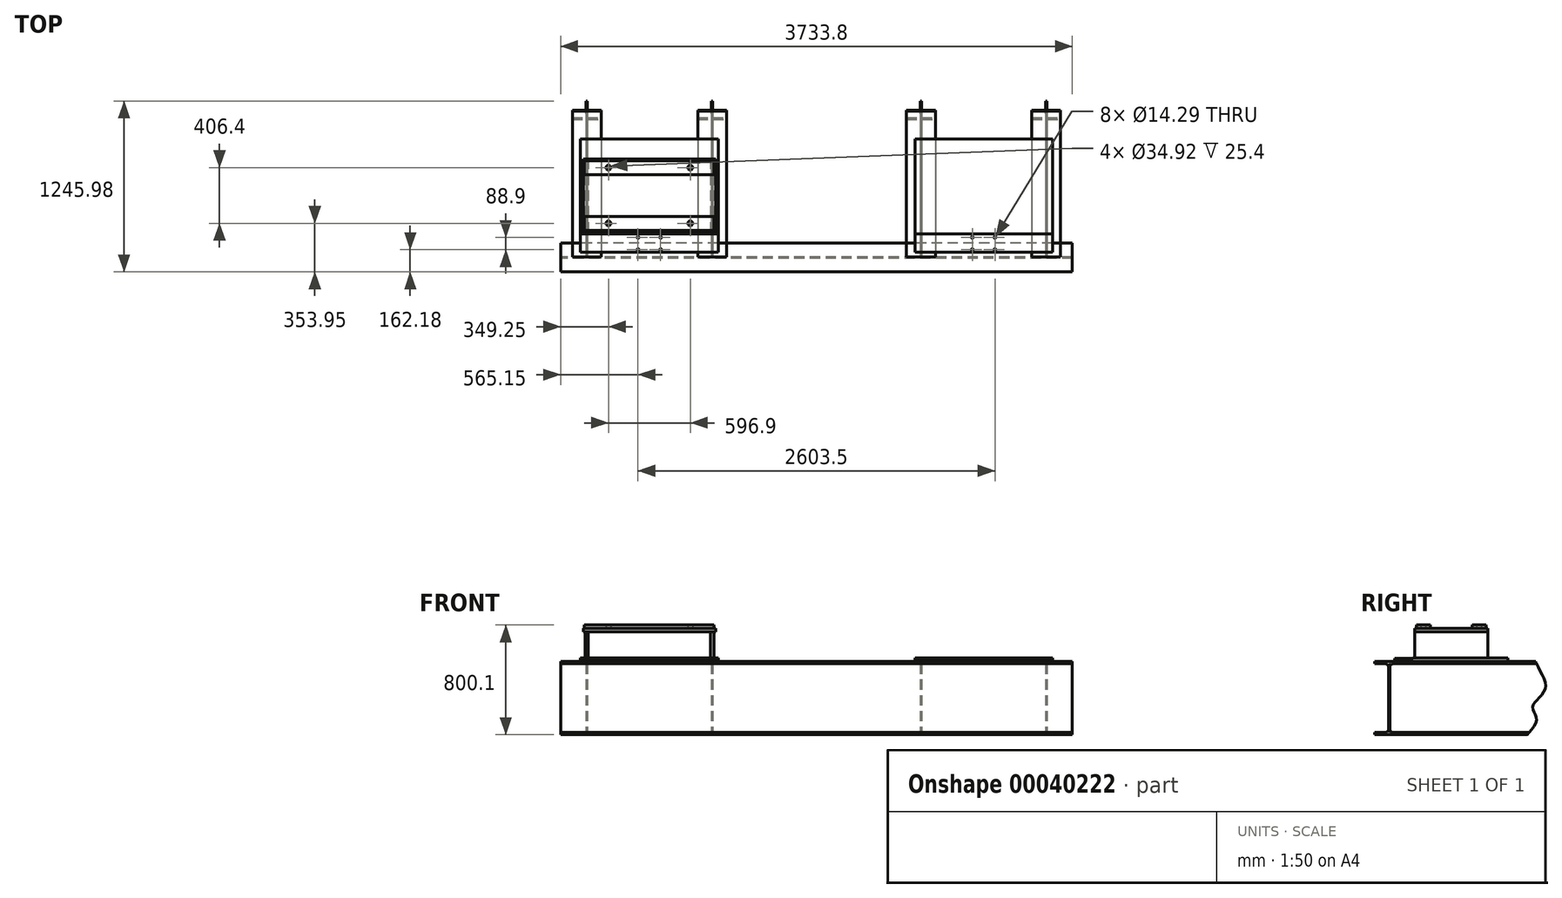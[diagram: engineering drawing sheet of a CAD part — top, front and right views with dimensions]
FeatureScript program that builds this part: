
annotation { "Feature Type Name" : "Feature", "Feature Type Description" : "" }
export const myFeature = defineFeature(function(context is Context, id is Id, definition is map)
    precondition{}
    {
        {
            var Q0;
            Q0=qCreatedBy(makeId("Top.planeOp"),FACE);
            var sketch = newSketch(context, id + "F0", { "sketchPlane" : qUnion([Q0])});
            skLineSegment(sketch, "E0", {"start": v(0, 102.84) * mm, "end": v(0, -93.54) * mm, "construction": true});
            skLineSegment(sketch, "E1.0", {"start": v(-1219.2, 102.84) * mm, "end": v(-1219.2, -93.54) * mm, "construction": true});
            skLineSegment(sketch, "E2", {"start": v(-1060.57, 0) * mm, "end": v(-1402.82, 0) * mm, "construction": true});
            skLineSegment(sketch, "E3.0", {"start": v(-1720.85, 412.75) * mm, "end": v(-1720.85, -412.75) * mm});
            skLineSegment(sketch, "E4.0", {"start": v(-717.55, -412.75) * mm, "end": v(-1720.85, -412.75) * mm});
            skLineSegment(sketch, "E5.MirrorCS", {"start": v(-717.55, 412.75) * mm, "end": v(-717.55, -412.75) * mm});
            skLineSegment(sketch, "E6.MirrorCS", {"start": v(-717.55, 412.75) * mm, "end": v(-1720.85, 412.75) * mm});
            skPoint(sketch, "E7.orphan", {"position": v(-1402.82, -412.75) * mm});
            skPoint(sketch, "E8.orphan", {"position": v(-1402.82, 412.75) * mm});
            skPoint(sketch, "E9.orphan", {"position": v(-1060.57, 412.75) * mm});
            skPoint(sketch, "E10.orphan", {"position": v(-1060.57, -412.75) * mm});
            skPoint(sketch, "E11.orphan", {"position": v(-1720.85, 102.84) * mm});
            skPoint(sketch, "E12.orphan", {"position": v(-1720.85, -93.54) * mm});
            skPoint(sketch, "E13.orphan", {"position": v(-717.55, -93.54) * mm});
            skPoint(sketch, "E14.orphan", {"position": v(-717.55, 102.84) * mm});
            skSolve(sketch);
        }
        {
            var Q0;
            Q0 = qSketchRegion(id + "F0", true);
            extrude(context, id + "F1", {"entities" : qUnion([Q0]), "oppositeDirection" : true, "depth" : 25.4 * mm});
        }
        {
            var Q0;
            Q0=makeQuery(id+"F1.opExtrude","SWEPT_FACE",FACE,{"disambiguationData":[OSD([sQuery(id+"F0.wireOp",EDGE,"E3.0")])]});
            var sketch = newSketch(context, id + "F2", { "sketchPlane" : qUnion([Q0])});
            skLineSegment(sketch, "E15", {"start": v(0, 139.77) * mm, "end": v(0, -170.54) * mm, "construction": true});
            skPoint(sketch, "E15.startSnap0", {"position": v(0, 0) * mm});
            skLineSegment(sketch, "E16.0", {"start": v(-412.75, 0) * mm, "end": v(412.75, 0) * mm, "construction": true});
            skLineSegment(sketch, "E17.0", {"start": v(279.4, 139.77) * mm, "end": v(279.4, -170.54) * mm, "construction": true});
            skLineSegment(sketch, "E18.0", {"start": v(-412.75, -3.18) * mm, "end": v(412.75, -3.18) * mm, "construction": true});
            skLineSegment(sketch, "E19.bottom", {"start": v(279.4, -3.18) * mm, "end": v(422.05, -3.18) * mm});
            skLineSegment(sketch, "E19.top", {"start": v(279.4, 13.88) * mm, "end": v(422.05, 13.88) * mm});
            skLineSegment(sketch, "E19.left", {"start": v(279.4, -3.18) * mm, "end": v(279.4, 13.88) * mm});
            skLineSegment(sketch, "E19.right", {"start": v(422.05, -3.18) * mm, "end": v(422.05, 13.88) * mm});
            skSolve(sketch);
        }
        {
            var Q0;
            Q0 = qSketchRegion(id + "F2", true);
            extrude(context, id + "F3", {"entities" : qUnion([Q0]), "operationType" : NewBodyOperationType.REMOVE, "endBound" : BoundingType.THROUGH_ALL, "oppositeDirection" : true, "depth" : 25.4 * mm});
        }
        {
            var Q0;
            Q0=makeQuery(id+"F0.imprint","IMPRINT",FACE,{"disambiguationData":[TD([[makeQuery(id+"F0.imprint","IMPRINT",EDGE,{"derivedFrom":sQuery(id+"F0.wireOp",EDGE,"E3.0")}),1.0]])]});
            cPlane(context, id + "F4", {"entities" : qUnion([Q0]), "cplaneType" : CPlaneType.OFFSET, "offset" : 215.9 * mm, "width" : 152.4 * mm, "height" : 152.4 * mm});
        }
        {
            var Q0;
            Q0=qCreatedBy(id+"F4.planeOp",FACE);
            var sketch = newSketch(context, id + "F5", { "sketchPlane" : qUnion([Q0])});
            skLineSegment(sketch, "E20.1", {"start": v(-1060.57, 0) * mm, "end": v(-1402.82, 0) * mm, "construction": true});
            skLineSegment(sketch, "E20.2", {"start": v(-1219.2, 102.84) * mm, "end": v(-1219.2, -93.54) * mm, "construction": true});
            skLineSegment(sketch, "E21.0", {"start": v(-736.6, 266.7) * mm, "end": v(-1701.8, 266.7) * mm});
            skLineSegment(sketch, "E22.0", {"start": v(-1701.8, 266.7) * mm, "end": v(-1701.8, -266.7) * mm});
            skLineSegment(sketch, "E23.MirrorCS", {"start": v(-736.6, 266.7) * mm, "end": v(-736.6, -266.7) * mm});
            skLineSegment(sketch, "E24.MirrorCS", {"start": v(-736.6, -266.7) * mm, "end": v(-1701.8, -266.7) * mm});
            skPoint(sketch, "E25.orphan", {"position": v(-1060.57, 266.7) * mm});
            skPoint(sketch, "E26.orphan", {"position": v(-736.6, 102.84) * mm});
            skPoint(sketch, "E27.orphan", {"position": v(-736.6, -93.54) * mm});
            skPoint(sketch, "E28.orphan", {"position": v(-1060.57, -266.7) * mm});
            skPoint(sketch, "E29.orphan", {"position": v(-1402.82, -266.7) * mm});
            skPoint(sketch, "E30.orphan", {"position": v(-1701.8, -93.54) * mm});
            skPoint(sketch, "E31.orphan", {"position": v(-1701.8, 102.84) * mm});
            skPoint(sketch, "E32.orphan", {"position": v(-1402.82, 266.7) * mm});
            skSolve(sketch);
        }
        {
            var Q0;
            Q0 = qSketchRegion(id + "F5", true);
            extrude(context, id + "F6", {"entities" : qUnion([Q0]), "oppositeDirection" : true, "depth" : 25.4 * mm});
        }
        {
            var Q0;
            Q0=makeQuery(id+"F6.opExtrude","CAP_FACE",FACE,{"disambiguationData":[OSD([sQuery(id+"F5.wireOp",EDGE,"E21.0"),sQuery(id+"F5.wireOp",EDGE,"E22.0"),sQuery(id+"F5.wireOp",EDGE,"E23.MirrorCS"),sQuery(id+"F5.wireOp",EDGE,"E24.MirrorCS")])],"isStart":true});
            var sketch = newSketch(context, id + "F7", { "sketchPlane" : qUnion([Q0])});
            skLineSegment(sketch, "E33", {"start": v(-736.6, 0) * mm, "end": v(-1701.8, 0) * mm, "construction": true});
            skLineSegment(sketch, "E34", {"start": v(-1219.2, 266.7) * mm, "end": v(-1219.2, -266.7) * mm, "construction": true});
            skLineSegment(sketch, "E35.0", {"start": v(-736.6, 152.4) * mm, "end": v(-1701.8, 152.4) * mm, "construction": true});
            skLineSegment(sketch, "E36.0", {"start": v(-736.6, 254) * mm, "end": v(-1701.8, 254) * mm, "construction": true});
            skLineSegment(sketch, "E37.0", {"start": v(-1692.27, 266.7) * mm, "end": v(-1692.27, -266.7) * mm, "construction": true});
            skLineSegment(sketch, "E38.bottom", {"start": v(-1692.27, 254) * mm, "end": v(-746.12, 254) * mm});
            skLineSegment(sketch, "E38.top", {"start": v(-1692.27, 152.4) * mm, "end": v(-746.12, 152.4) * mm});
            skLineSegment(sketch, "E38.left", {"start": v(-1692.27, 254) * mm, "end": v(-1692.27, 152.4) * mm});
            skLineSegment(sketch, "E38.right", {"start": v(-746.12, 254) * mm, "end": v(-746.12, 152.4) * mm});
            skLineSegment(sketch, "E39.MirrorCS", {"start": v(-736.6, -254) * mm, "end": v(-1701.8, -254) * mm});
            skLineSegment(sketch, "E40.MirrorCS", {"start": v(-736.6, -152.4) * mm, "end": v(-1701.8, -152.4) * mm});
            skLineSegment(sketch, "E41.MirrorCS", {"start": v(-1692.27, -254) * mm, "end": v(-1692.27, -152.4) * mm});
            skLineSegment(sketch, "E42.MirrorCS", {"start": v(-1692.27, -152.4) * mm, "end": v(-746.12, -152.4) * mm});
            skLineSegment(sketch, "E43.MirrorCS", {"start": v(-1692.27, -254) * mm, "end": v(-746.12, -254) * mm});
            skLineSegment(sketch, "E44.MirrorCS", {"start": v(-746.12, -254) * mm, "end": v(-746.12, -152.4) * mm});
            skLineSegment(sketch, "E45", {"start": v(-1692.27, 203.2) * mm, "end": v(-746.12, 203.2) * mm, "construction": true});
            skLineSegment(sketch, "E46.0", {"start": v(-1517.65, 266.7) * mm, "end": v(-1517.65, -266.7) * mm, "construction": true});
            skCircle(sketch, "E47", {"center": v(-1517.65, 203.2) * mm, "radius": 17.46 * mm});
            skCircle(sketch, "E48.MirrorC", {"center": v(-920.75, 203.2) * mm, "radius": 17.46 * mm});
            skCircle(sketch, "E49.MirrorC", {"center": v(-920.75, -203.2) * mm, "radius": 17.46 * mm});
            skCircle(sketch, "E50.MirrorC", {"center": v(-1517.65, -203.2) * mm, "radius": 17.46 * mm});
            skSolve(sketch);
        }
        {
            var Q0;
            Q0 = qSketchRegion(id + "F7", true);
            extrude(context, id + "F8", {"entities" : qUnion([Q0]), "operationType" : NewBodyOperationType.ADD, "depth" : 25.4 * mm});
        }
        {
            var Q0;
            Q0=makeQuery(id+"F0.imprint","IMPRINT",FACE,{"disambiguationData":[TD([[makeQuery(id+"F0.imprint","IMPRINT",EDGE,{"derivedFrom":sQuery(id+"F0.wireOp",EDGE,"E3.0")}),1.0]])]});
            var sketch = newSketch(context, id + "F9", { "sketchPlane" : qUnion([Q0])});
            skLineSegment(sketch, "E51.0", {"start": v(-1219.2, 102.84) * mm, "end": v(-1219.2, -93.54) * mm, "construction": true});
            skLineSegment(sketch, "E52.0", {"start": v(-736.6, 266.7) * mm, "end": v(-1701.8, 266.7) * mm, "construction": true});
            skLineSegment(sketch, "E53.0", {"start": v(-736.6, -266.7) * mm, "end": v(-1701.8, -266.7) * mm, "construction": true});
            skLineSegment(sketch, "E54.0", {"start": v(-1663.7, 266.7) * mm, "end": v(-1663.7, -93.54) * mm, "construction": true});
            skLineSegment(sketch, "E55.0", {"start": v(-1689.1, 102.84) * mm, "end": v(-1689.1, -93.54) * mm, "construction": true});
            skLineSegment(sketch, "E56.bottom", {"start": v(-1663.7, 266.7) * mm, "end": v(-1689.1, 266.7) * mm});
            skLineSegment(sketch, "E56.top", {"start": v(-1663.7, -266.7) * mm, "end": v(-1689.1, -266.7) * mm});
            skLineSegment(sketch, "E56.left", {"start": v(-1663.7, 266.7) * mm, "end": v(-1663.7, -266.7) * mm});
            skLineSegment(sketch, "E56.right", {"start": v(-1689.1, 266.7) * mm, "end": v(-1689.1, -266.7) * mm});
            skLineSegment(sketch, "E57.MirrorCS", {"start": v(-774.7, -266.7) * mm, "end": v(-749.3, -266.7) * mm});
            skLineSegment(sketch, "E58.MirrorCS", {"start": v(-774.7, 266.7) * mm, "end": v(-749.3, 266.7) * mm});
            skLineSegment(sketch, "E59.MirrorCS", {"start": v(-749.3, 102.84) * mm, "end": v(-749.3, -93.54) * mm});
            skLineSegment(sketch, "E60.MirrorCS", {"start": v(-774.7, 266.7) * mm, "end": v(-774.7, -93.54) * mm});
            skLineSegment(sketch, "E61.MirrorCS", {"start": v(-749.3, 266.7) * mm, "end": v(-749.3, -266.7) * mm});
            skLineSegment(sketch, "E62.MirrorCS", {"start": v(-774.7, 266.7) * mm, "end": v(-774.7, -266.7) * mm});
            skSolve(sketch);
        }
        {
            var Q0;
            Q0 = qSketchRegion(id + "F9", true);
            var Q1;
            Q1=makeQuery(id+"F6.opExtrude","CAP_FACE",FACE,{"disambiguationData":[OSD([sQuery(id+"F5.wireOp",EDGE,"E21.0"),sQuery(id+"F5.wireOp",EDGE,"E22.0"),sQuery(id+"F5.wireOp",EDGE,"E23.MirrorCS"),sQuery(id+"F5.wireOp",EDGE,"E24.MirrorCS")])],"isStart":false});
            extrude(context, id + "F10", {"entities" : qUnion([Q0]), "endBound" : BoundingType.UP_TO_SURFACE, "endBoundEntityFace" : qUnion([Q1]), "depth" : 25.4 * mm});
        }
        {
            var Q0;
            Q0=makeQuery(id+"F0.imprint","IMPRINT",FACE,{"disambiguationData":[TD([[makeQuery(id+"F0.imprint","IMPRINT",EDGE,{"derivedFrom":sQuery(id+"F0.wireOp",EDGE,"E3.0")}),1.0]])]});
            var sketch = newSketch(context, id + "F11", { "sketchPlane" : qUnion([Q0])});
            skLineSegment(sketch, "E63.0", {"start": v(-1219.2, 102.84) * mm, "end": v(-1219.2, -412.75) * mm, "construction": true});
            skLineSegment(sketch, "E64.0", {"start": v(-717.55, -412.75) * mm, "end": v(-1720.85, -412.75) * mm, "construction": true});
            skPoint(sketch, "E65.orphan", {"position": v(-1219.2, -93.54) * mm});
            skLineSegment(sketch, "E66.0", {"start": v(-1060.57, 0) * mm, "end": v(-1402.82, 0) * mm, "construction": true});
            skLineSegment(sketch, "E67.0", {"start": v(-1060.57, -306.07) * mm, "end": v(-1402.82, -306.07) * mm, "construction": true});
            skLineSegment(sketch, "E68.0", {"start": v(-1060.57, -394.97) * mm, "end": v(-1402.82, -394.97) * mm, "construction": true});
            skLineSegment(sketch, "E69.0", {"start": v(-1301.75, 102.84) * mm, "end": v(-1301.75, -412.75) * mm, "construction": true});
            skLineSegment(sketch, "E70.0", {"start": v(-1136.65, 102.84) * mm, "end": v(-1136.65, -412.75) * mm, "construction": true});
            skPoint(sketch, "E71", {"position": v(-1136.65, -306.07) * mm});
            skPoint(sketch, "E72", {"position": v(-1136.65, -394.97) * mm});
            skPoint(sketch, "E73", {"position": v(-1301.75, -394.97) * mm});
            skPoint(sketch, "E74", {"position": v(-1301.75, -306.07) * mm});
            skSolve(sketch);
        }
        {
            var Q0;
            Q0=sQuery(id+"F11.wireOp",VERTEX,"E71");
            var Q1;
            Q1=sQuery(id+"F11.wireOp",VERTEX,"E72");
            var Q2;
            Q2=sQuery(id+"F11.wireOp",VERTEX,"E74");
            var Q3;
            Q3=sQuery(id+"F11.wireOp",VERTEX,"E73");
            var Q4;
            Q4=makeQuery(id+"F1.opExtrude","SWEPT_BODY",BODY,{"disambiguationData":[OSD([sQuery(id+"F0.wireOp",EDGE,"E3.0"),sQuery(id+"F0.wireOp",EDGE,"E4.0"),sQuery(id+"F0.wireOp",EDGE,"E5.MirrorCS"),sQuery(id+"F0.wireOp",EDGE,"E6.MirrorCS")])]});
            hole(context, id + "F12", {"style" : HoleStyle.SIMPLE, "holeDiameter" : 14.29 * mm, "endStyle" : HoleEndStyle.THROUGH, "locations" : qUnion([Q0, Q1, Q2, Q3]), "scope" : qUnion([Q4])});
        }
        {
            var Q0;
            Q0=qCreatedBy(makeId("Right.planeOp"),FACE);
            var sketch = newSketch(context, id + "F13", { "sketchPlane" : qUnion([Q0])});
            skLineSegment(sketch, "E75", {"start": v(0, 291.52) * mm, "end": v(0, -174.65) * mm, "construction": true});
            skLineSegment(sketch, "E76.0", {"start": v(-452.37, -25.4) * mm, "end": v(-452.37, -558.8) * mm, "construction": true});
            skLineSegment(sketch, "E77.0", {"start": v(412.75, -25.4) * mm, "end": v(-452.37, -25.4) * mm, "construction": true});
            skPoint(sketch, "E78.orphan", {"position": v(-412.75, -25.4) * mm});
            skLineSegment(sketch, "E79.0", {"start": v(-347.6, -558.8) * mm, "end": v(-452.37, -558.8) * mm});
            skLineSegment(sketch, "E80.0", {"start": v(-347.6, 291.52) * mm, "end": v(-347.6, -41.02) * mm});
            skLineSegment(sketch, "E81.bottom", {"start": v(-347.6, -558.8) * mm, "end": v(-557.15, -558.8) * mm});
            skLineSegment(sketch, "E81.top", {"start": v(-347.6, -25.4) * mm, "end": v(-557.15, -25.4) * mm});
            skLineSegment(sketch, "E81.left", {"start": v(-347.6, -558.8) * mm, "end": v(-347.6, -543.18) * mm});
            skLineSegment(sketch, "E81.right", {"start": v(-557.15, -558.8) * mm, "end": v(-557.15, -543.18) * mm});
            skLineSegment(sketch, "E82.0", {"start": v(-347.6, -41.02) * mm, "end": v(-421.9, -41.02) * mm});
            skLineSegment(sketch, "E83.0", {"start": v(-347.6, -543.18) * mm, "end": v(-421.9, -543.18) * mm});
            skLineSegment(sketch, "E84.1", {"start": v(-457.45, -66.42) * mm, "end": v(-457.45, -517.78) * mm});
            skLineSegment(sketch, "E85.1", {"start": v(-447.3, -66.42) * mm, "end": v(-447.3, -517.78) * mm});
            skLineSegment(sketch, "E86.trimOffspring", {"start": v(-557.15, -41.02) * mm, "end": v(-557.15, -25.4) * mm});
            skLineSegment(sketch, "E87.trimOffspring", {"start": v(-482.85, -41.02) * mm, "end": v(-557.15, -41.02) * mm});
            skLineSegment(sketch, "E88.trimOffspring", {"start": v(-347.6, -543.18) * mm, "end": v(-347.6, -558.8) * mm});
            skLineSegment(sketch, "E89.trimOffspring", {"start": v(-347.6, -41.02) * mm, "end": v(-347.6, -25.4) * mm});
            skLineSegment(sketch, "E90.trimOffspring", {"start": v(-482.85, -543.18) * mm, "end": v(-557.15, -543.18) * mm});
            skPoint(sketch, "E91.visualSharp", {"position": v(-457.45, -41.02) * mm});
            skArc(sketch, "E91.filletArc", {"start": v(-457.45, -66.42) * mm, "mid": v(-464.9, -48.46) * mm, "end": v(-482.85, -41.02) * mm});
            skPoint(sketch, "E92.visualSharp", {"position": v(-447.3, -41.02) * mm});
            skArc(sketch, "E92.filletArc", {"start": v(-421.9, -41.02) * mm, "mid": v(-439.85, -48.46) * mm, "end": v(-447.3, -66.42) * mm});
            skPoint(sketch, "E93.visualSharp", {"position": v(-457.45, -543.18) * mm});
            skArc(sketch, "E93.filletArc", {"start": v(-482.85, -543.18) * mm, "mid": v(-464.9, -535.74) * mm, "end": v(-457.45, -517.78) * mm});
            skPoint(sketch, "E94.visualSharp", {"position": v(-447.3, -543.18) * mm});
            skArc(sketch, "E94.filletArc", {"start": v(-447.3, -517.78) * mm, "mid": v(-439.85, -535.74) * mm, "end": v(-421.9, -543.18) * mm});
            skSolve(sketch);
        }
        {
            var Q0;
            Q0 = qSketchRegion(id + "F13", true);
            extrude(context, id + "F14", {"entities" : qUnion([Q0]), "endBound" : BoundingType.SYMMETRIC, "depth" : 3733.8 * mm});
        }
        {
            var Q0;
            Q0=makeQuery(id+"F14.opExtrude","SWEPT_FACE",FACE,{"disambiguationData":[OSD([sQuery(id+"F13.wireOp",EDGE,"E85.1")])]});
            var sketch = newSketch(context, id + "F15", { "sketchPlane" : qUnion([Q0])});
            skLineSegment(sketch, "E95", {"start": v(0, 728.98) * mm, "end": v(0, -1136.59) * mm, "construction": true});
            skLineSegment(sketch, "E96.0", {"start": v(762, 728.98) * mm, "end": v(762, -543.18) * mm, "construction": true});
            skLineSegment(sketch, "E97.0", {"start": v(1676.4, 728.98) * mm, "end": v(1676.4, -1136.59) * mm, "construction": true});
            skLineSegment(sketch, "E98.0", {"start": v(-1866.9, -25.4) * mm, "end": v(0, -25.4) * mm});
            skLineSegment(sketch, "E99.0", {"start": v(-1866.9, -41.02) * mm, "end": v(0, -41.02) * mm});
            skLineSegment(sketch, "E100.0", {"start": v(-1866.9, -543.18) * mm, "end": v(0, -543.18) * mm});
            skLineSegment(sketch, "E101.0", {"start": v(-1866.9, -558.8) * mm, "end": v(0, -558.8) * mm});
            skLineSegment(sketch, "E102.0", {"start": v(657.23, -25.4) * mm, "end": v(657.23, -41.02) * mm});
            skLineSegment(sketch, "E103", {"start": v(762, -808.54) * mm, "end": v(1676.4, -808.54) * mm, "construction": true});
            skLineSegment(sketch, "E104", {"start": v(1219.2, -808.54) * mm, "end": v(1219.2, -673.05) * mm, "construction": true});
            skLineSegment(sketch, "E105.trimOffspring", {"start": v(657.23, -543.18) * mm, "end": v(657.23, -558.8) * mm});
            skLineSegment(sketch, "E106.trimOffspring", {"start": v(657.23, -25.4) * mm, "end": v(866.77, -25.4) * mm});
            skLineSegment(sketch, "E107.trimOffspring", {"start": v(657.23, -41.02) * mm, "end": v(866.77, -41.02) * mm});
            skLineSegment(sketch, "E108.trimOffspring", {"start": v(657.22, -543.18) * mm, "end": v(866.78, -543.18) * mm});
            skLineSegment(sketch, "E109.trimOffspring", {"start": v(657.23, -558.8) * mm, "end": v(866.78, -558.8) * mm});
            skLineSegment(sketch, "E110.trimOffspring", {"start": v(756.92, -41.02) * mm, "end": v(756.92, -543.18) * mm});
            skLineSegment(sketch, "E111.trimOffspring", {"start": v(762, -558.8) * mm, "end": v(762, -1136.59) * mm, "construction": true});
            skLineSegment(sketch, "E112.MirrorCS", {"start": v(866.78, -543.18) * mm, "end": v(866.78, -558.8) * mm});
            skLineSegment(sketch, "E113.MirrorCS", {"start": v(767.08, -41.02) * mm, "end": v(767.08, -543.18) * mm});
            skLineSegment(sketch, "E114.MirrorCS", {"start": v(866.77, -25.4) * mm, "end": v(866.77, -41.02) * mm});
            skLineSegment(sketch, "E115.MirrorCS", {"start": v(1781.18, -543.18) * mm, "end": v(1781.18, -558.8) * mm});
            skLineSegment(sketch, "E116.MirrorCS", {"start": v(1781.18, -25.4) * mm, "end": v(1781.18, -41.02) * mm});
            skLineSegment(sketch, "E117.MirrorCS", {"start": v(1571.63, -543.18) * mm, "end": v(1571.63, -558.8) * mm});
            skLineSegment(sketch, "E118.MirrorCS", {"start": v(1571.63, -25.4) * mm, "end": v(1571.63, -41.02) * mm});
            skLineSegment(sketch, "E119.MirrorCS", {"start": v(1671.32, -41.02) * mm, "end": v(1671.32, -543.18) * mm});
            skLineSegment(sketch, "E120.MirrorCS", {"start": v(1681.48, -41.02) * mm, "end": v(1681.48, -543.18) * mm});
            skLineSegment(sketch, "E121.trimOffspring", {"start": v(1571.63, -41.02) * mm, "end": v(1781.18, -41.02) * mm});
            skLineSegment(sketch, "E122.trimOffspring", {"start": v(1571.63, -25.4) * mm, "end": v(1781.18, -25.4) * mm});
            skLineSegment(sketch, "E123.trimOffspring", {"start": v(1571.63, -543.18) * mm, "end": v(1781.18, -543.18) * mm});
            skLineSegment(sketch, "E124.trimOffspring", {"start": v(1571.63, -558.8) * mm, "end": v(1781.18, -558.8) * mm});
            skPoint(sketch, "E125.orphan", {"position": v(1866.9, -558.8) * mm});
            skPoint(sketch, "E126.orphan", {"position": v(1866.9, -543.18) * mm});
            skPoint(sketch, "E127.orphan", {"position": v(1866.9, -41.02) * mm});
            skPoint(sketch, "E128.orphan", {"position": v(1866.9, -25.4) * mm});
            skSolve(sketch);
        }
        {
            var Q0;
            Q0 = qSketchRegion(id + "F15", true);
            extrude(context, id + "F16", {"entities" : qUnion([Q0]), "depth" : 3048 * mm});
        }
        {
            var Q0;
            Q0=makeQuery(id+"F1.opExtrude","SWEPT_BODY",BODY,{"disambiguationData":[OSD([sQuery(id+"F0.wireOp",EDGE,"E3.0"),sQuery(id+"F0.wireOp",EDGE,"E4.0"),sQuery(id+"F0.wireOp",EDGE,"E5.MirrorCS"),sQuery(id+"F0.wireOp",EDGE,"E6.MirrorCS")])]});
            var Q1;
            Q1=makeQuery(id+"F16.opExtrude","SWEPT_BODY",BODY,{"disambiguationData":[OSD([sQuery(id+"F15.wireOp",EDGE,"E115.MirrorCS"),sQuery(id+"F15.wireOp",EDGE,"E116.MirrorCS"),sQuery(id+"F15.wireOp",EDGE,"E117.MirrorCS"),sQuery(id+"F15.wireOp",EDGE,"E118.MirrorCS"),sQuery(id+"F15.wireOp",EDGE,"E119.MirrorCS"),sQuery(id+"F15.wireOp",EDGE,"E120.MirrorCS"),sQuery(id+"F15.wireOp",EDGE,"E121.trimOffspring"),sQuery(id+"F15.wireOp",EDGE,"E122.trimOffspring"),sQuery(id+"F15.wireOp",EDGE,"E123.trimOffspring"),sQuery(id+"F15.wireOp",EDGE,"E124.trimOffspring")])]});
            var Q2;
            Q2=makeQuery(id+"F16.opExtrude","SWEPT_BODY",BODY,{"disambiguationData":[OSD([sQuery(id+"F15.wireOp",EDGE,"E102.0"),sQuery(id+"F15.wireOp",EDGE,"E105.trimOffspring"),sQuery(id+"F15.wireOp",EDGE,"E106.trimOffspring"),sQuery(id+"F15.wireOp",EDGE,"E107.trimOffspring"),sQuery(id+"F15.wireOp",EDGE,"E108.trimOffspring"),sQuery(id+"F15.wireOp",EDGE,"E109.trimOffspring"),sQuery(id+"F15.wireOp",EDGE,"E110.trimOffspring"),sQuery(id+"F15.wireOp",EDGE,"E112.MirrorCS"),sQuery(id+"F15.wireOp",EDGE,"E113.MirrorCS"),sQuery(id+"F15.wireOp",EDGE,"E114.MirrorCS")])]});
            var Q3;
            Q3=qCreatedBy(makeId("Right.planeOp"),FACE);
            mirror(context, id + "F17", {"entities" : qUnion([Q0, Q1, Q2]), "mirrorPlane" : qUnion([Q3])});
        }
        {
            var Q0;
            Q0=qCreatedBy(makeId("Right.planeOp"),FACE);
            var sketch = newSketch(context, id + "F18", { "sketchPlane" : qUnion([Q0])});
            skFitSpline(sketch, "E129", {"points": [v(708.27, 103.39) * mm, v(608.62, 0) * mm, v(687.83, -215.99) * mm, v(595.85, -351.4) * mm, v(621.4, -461.27) * mm, v(516.64, -622.23) * mm, v(1321.46, -698.88) * mm, v(2655.17, -691.21) * mm, v(2598.96, 128.94) * mm, v(2052.2, 246.47) * mm, v(1372.56, 203.03) * mm, v(708.27, 103.39) * mm]});
            skSolve(sketch);
        }
        {
            var Q0;
            Q0 = qSketchRegion(id + "F18", true);
            extrude(context, id + "F19", {"entities" : qUnion([Q0]), "operationType" : NewBodyOperationType.REMOVE, "endBound" : BoundingType.SYMMETRIC, "oppositeDirection" : true, "depth" : 5080 * mm});
        }
    });
